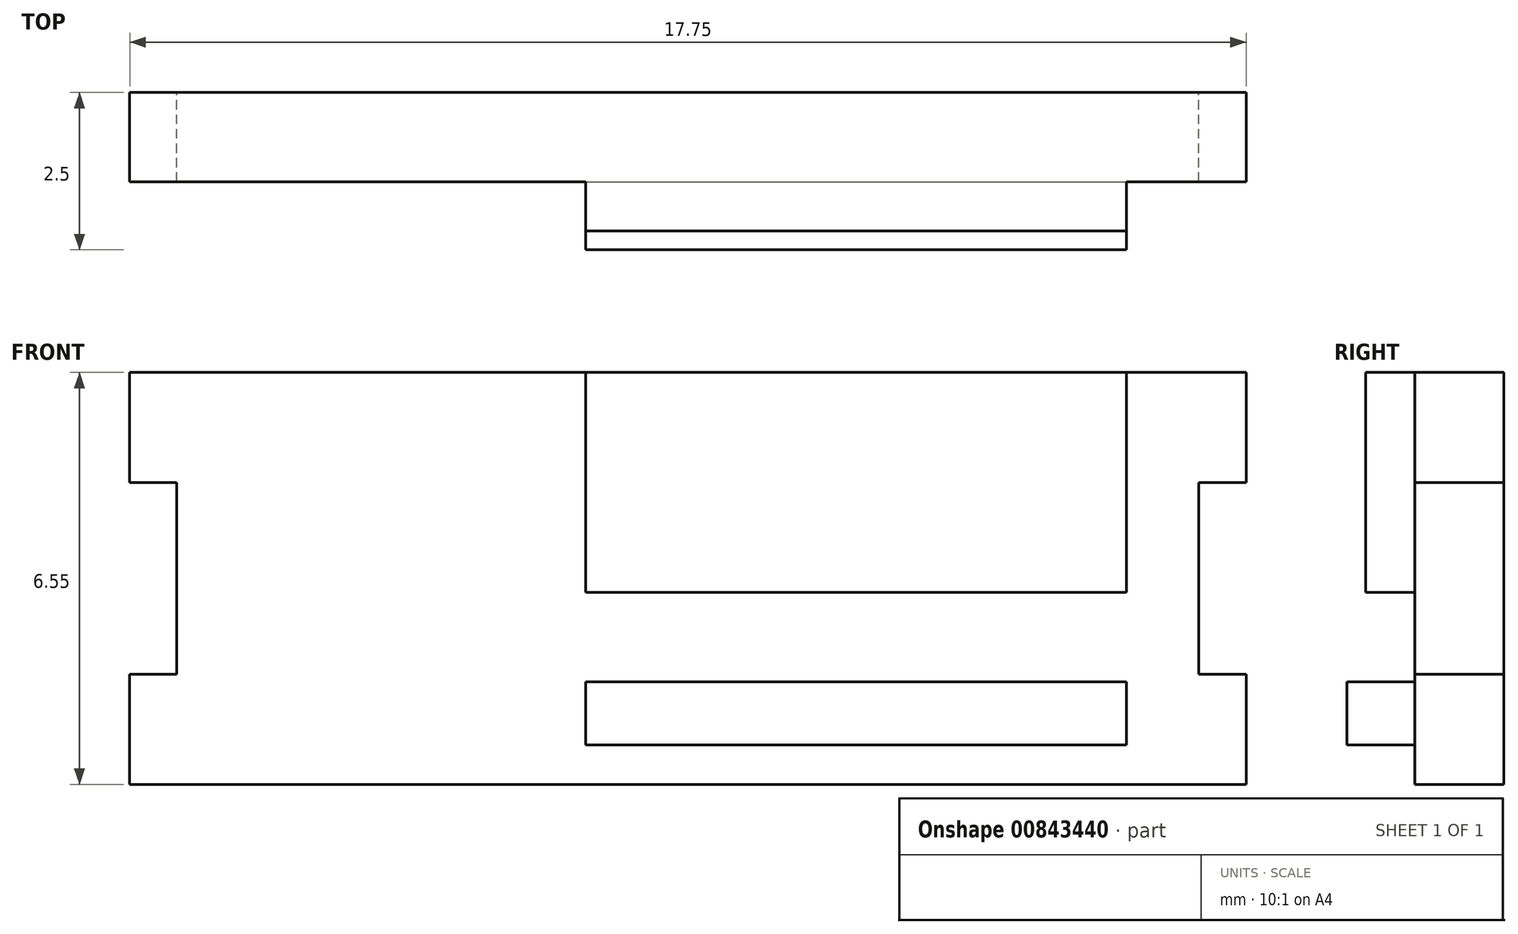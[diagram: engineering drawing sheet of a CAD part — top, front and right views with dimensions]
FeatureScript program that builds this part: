
annotation { "Feature Type Name" : "Feature", "Feature Type Description" : "" }
export const myFeature = defineFeature(function(context is Context, id is Id, definition is map)
    precondition{}
    {
        {
            var Q0;
            Q0=qCreatedBy(makeId("Front.planeOp"),FACE);
            var sketch = newSketch(context, id + "F0", { "sketchPlane" : qUnion([Q0])});
            skLineSegment(sketch, "E0.bottom", {"start": v(-14.12, 25.74) * mm, "end": v(3.63, 25.74) * mm});
            skLineSegment(sketch, "E0.top", {"start": v(-14.12, 19.2) * mm, "end": v(3.63, 19.2) * mm});
            skLineSegment(sketch, "E1.left", {"start": v(-13.37, 24) * mm, "end": v(-13.37, 20.94) * mm});
            skLineSegment(sketch, "E1.right", {"start": v(2.88, 24) * mm, "end": v(2.88, 20.94) * mm});
            skLineSegment(sketch, "E2", {"start": v(-13.37, 24) * mm, "end": v(-14.12, 24) * mm});
            skLineSegment(sketch, "E3", {"start": v(-14.12, 20.94) * mm, "end": v(-13.37, 20.94) * mm});
            skLineSegment(sketch, "E4", {"start": v(-14.12, 25.74) * mm, "end": v(-14.12, 24) * mm});
            skLineSegment(sketch, "E5", {"start": v(-14.12, 20.94) * mm, "end": v(-14.12, 19.2) * mm});
            skLineSegment(sketch, "E6", {"start": v(2.88, 24) * mm, "end": v(3.63, 24) * mm});
            skLineSegment(sketch, "E7", {"start": v(2.88, 20.94) * mm, "end": v(3.63, 20.94) * mm});
            skLineSegment(sketch, "E8", {"start": v(3.63, 25.74) * mm, "end": v(3.63, 24) * mm});
            skLineSegment(sketch, "E9", {"start": v(3.63, 19.2) * mm, "end": v(3.63, 20.94) * mm});
            skSolve(sketch);
        }
        {
            var Q0;
            Q0=makeQuery(id+"F0.imprint","IMPRINT",FACE,{"disambiguationData":[TD([[makeQuery(id+"F0.imprint","IMPRINT",EDGE,{"derivedFrom":sQuery(id+"F0.wireOp",EDGE,"E0.bottom")}),-1.0]])]});
            var sketch = newSketch(context, id + "F1", { "sketchPlane" : qUnion([Q0])});
            skLineSegment(sketch, "E10.bottom", {"start": v(1.73, 19.82) * mm, "end": v(-6.87, 19.82) * mm});
            skLineSegment(sketch, "E10.top", {"start": v(1.73, 20.82) * mm, "end": v(-6.87, 20.82) * mm});
            skLineSegment(sketch, "E10.left", {"start": v(1.73, 19.82) * mm, "end": v(1.73, 20.82) * mm});
            skLineSegment(sketch, "E10.right", {"start": v(-6.87, 19.82) * mm, "end": v(-6.87, 20.82) * mm});
            skSolve(sketch);
        }
        {
            var Q0;
            Q0=makeQuery(id+"F0.imprint","IMPRINT",FACE,{"disambiguationData":[TD([[makeQuery(id+"F0.imprint","IMPRINT",EDGE,{"derivedFrom":sQuery(id+"F0.wireOp",EDGE,"E0.bottom")}),-1.0]])]});
            var sketch = newSketch(context, id + "F2", { "sketchPlane" : qUnion([Q0])});
            skLineSegment(sketch, "E11.bottom", {"start": v(-6.87, 25.74) * mm, "end": v(1.73, 25.74) * mm});
            skLineSegment(sketch, "E11.top", {"start": v(-6.87, 22.24) * mm, "end": v(1.73, 22.24) * mm});
            skLineSegment(sketch, "E11.left", {"start": v(-6.87, 25.74) * mm, "end": v(-6.87, 22.24) * mm});
            skLineSegment(sketch, "E11.right", {"start": v(1.73, 25.74) * mm, "end": v(1.73, 22.24) * mm});
            skSolve(sketch);
        }
        {
            var Q0;
            Q0=makeQuery(id+"F0.imprint","IMPRINT",FACE,{"disambiguationData":[TD([[makeQuery(id+"F0.imprint","IMPRINT",EDGE,{"derivedFrom":sQuery(id+"F0.wireOp",EDGE,"E0.bottom")}),-1.0]])]});
            extrude(context, id + "F3", {"entities" : qUnion([Q0]), "depth" : 1.42 * mm, "offsetDistance" : 25 * mm});
        }
        {
            var Q0;
            Q0 = qSketchRegion(id + "F1", true);
            extrude(context, id + "F4", {"entities" : qUnion([Q0]), "operationType" : NewBodyOperationType.ADD, "depth" : 2.5 * mm, "offsetDistance" : 25 * mm});
        }
        {
            var Q0;
            Q0 = qSketchRegion(id + "F2", true);
            extrude(context, id + "F5", {"entities" : qUnion([Q0]), "operationType" : NewBodyOperationType.ADD, "depth" : 2.2 * mm, "offsetDistance" : 25 * mm});
        }
    });
